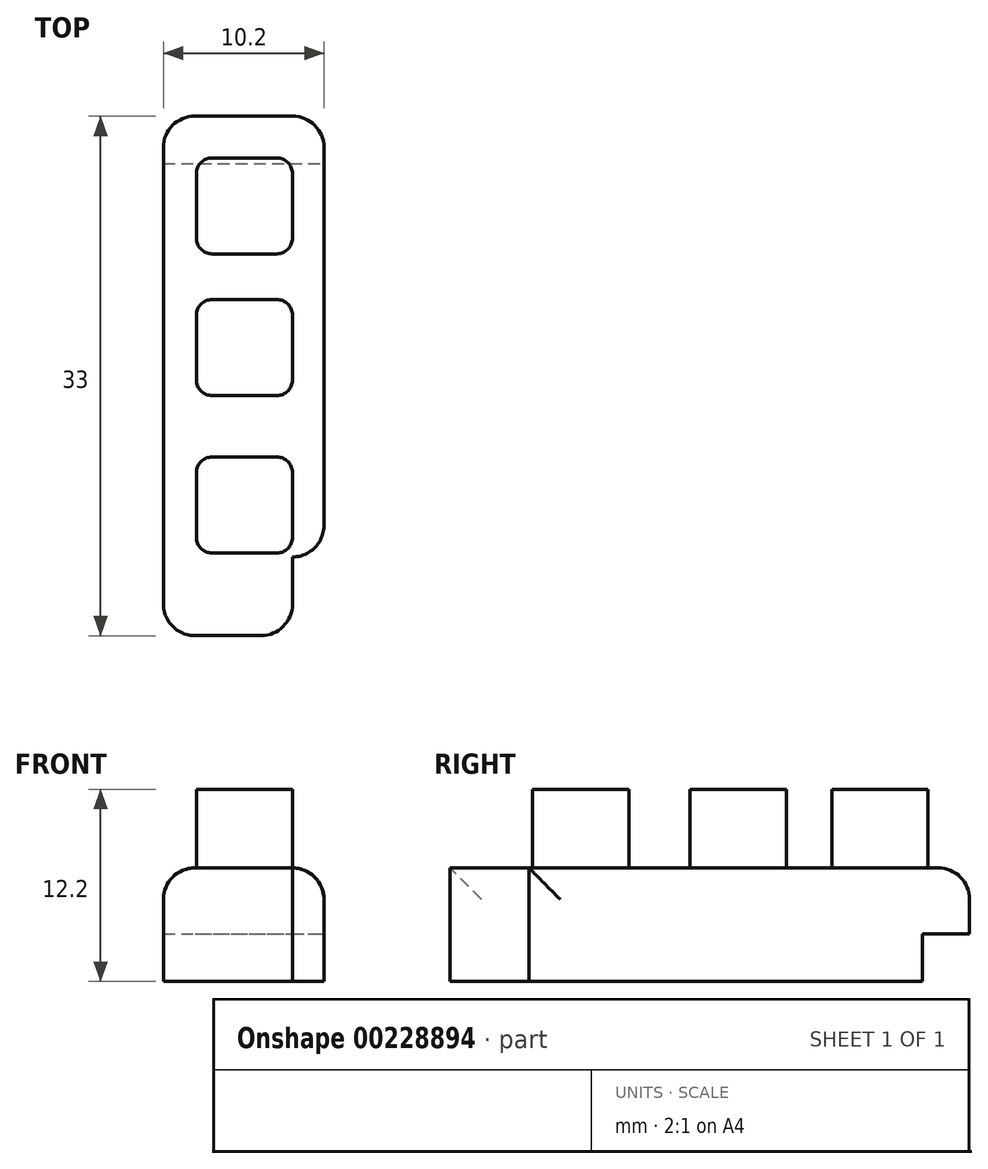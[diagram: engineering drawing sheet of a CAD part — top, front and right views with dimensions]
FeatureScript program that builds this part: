
annotation { "Feature Type Name" : "Feature", "Feature Type Description" : "" }
export const myFeature = defineFeature(function(context is Context, id is Id, definition is map)
    precondition{}
    {
        {
            var Q0;
            Q0=qCreatedBy(makeId("Top.planeOp"),FACE);
            var sketch = newSketch(context, id + "F0", { "sketchPlane" : qUnion([Q0])});
            skLineSegment(sketch, "E0.bottom", {"start": v(-1.8, 2.84) * mm, "end": v(4.4, 2.84) * mm});
            skLineSegment(sketch, "E0.left", {"start": v(-3.8, 0.84) * mm, "end": v(-3.8, -22.16) * mm});
            skLineSegment(sketch, "E0.right", {"start": v(6.4, 0.84) * mm, "end": v(6.4, -23.16) * mm});
            skPoint(sketch, "E1.visualSharp", {"position": v(-3.8, 2.84) * mm});
            skArc(sketch, "E1.filletArc", {"start": v(-1.8, 2.84) * mm, "mid": v(-3.22, 2.26) * mm, "end": v(-3.8, 0.84) * mm});
            skPoint(sketch, "E2.visualSharp", {"position": v(6.4, 2.84) * mm});
            skArc(sketch, "E2.filletArc", {"start": v(6.4, 0.84) * mm, "mid": v(5.8, 2.26) * mm, "end": v(4.4, 2.84) * mm});
            skPoint(sketch, "E3.visualSharp", {"position": v(6.4, -29.16) * mm});
            skLineSegment(sketch, "E4.top", {"start": v(-1.8, -30.16) * mm, "end": v(2.4, -30.16) * mm});
            skLineSegment(sketch, "E4.left", {"start": v(-3.8, -22.16) * mm, "end": v(-3.8, -28.16) * mm});
            skPoint(sketch, "E5.visualSharp", {"position": v(-3.8, -30.16) * mm});
            skArc(sketch, "E5.filletArc", {"start": v(-3.8, -28.16) * mm, "mid": v(-3.22, -29.57) * mm, "end": v(-1.8, -30.16) * mm});
            skLineSegment(sketch, "E6.bottom", {"start": v(4.4, -25.16) * mm, "end": v(4.4, -25.16) * mm});
            skLineSegment(sketch, "E6.right", {"start": v(4.4, -25.16) * mm, "end": v(4.4, -28.16) * mm});
            skPoint(sketch, "E7.visualSharp", {"position": v(6.4, -25.16) * mm});
            skArc(sketch, "E7.filletArc", {"start": v(4.4, -25.16) * mm, "mid": v(5.8, -24.57) * mm, "end": v(6.4, -23.16) * mm});
            skPoint(sketch, "E8.visualSharp", {"position": v(4.4, -30.16) * mm});
            skArc(sketch, "E8.filletArc", {"start": v(2.4, -30.16) * mm, "mid": v(3.8, -29.57) * mm, "end": v(4.4, -28.16) * mm});
            skSolve(sketch);
        }
        {
            var Q0;
            Q0 = qSketchRegion(id + "F0", true);
            extrude(context, id + "F1", {"entities" : qUnion([Q0]), "depth" : 7.2 * mm, "offsetDistance" : 25 * mm});
        }
        {
            var Q0;
            Q0=makeQuery(id+"F1.opExtrude","CAP_EDGE",EDGE,{"disambiguationData":[OSD([sQuery(id+"F0.wireOp",EDGE,"E0.left")])],"isStart":false});
            var Q1;
            Q1=makeQuery(id+"F1.opExtrude","CAP_EDGE",EDGE,{"disambiguationData":[OSD([sQuery(id+"F0.wireOp",EDGE,"E1.filletArc")])],"isStart":false});
            var Q2;
            Q2=makeQuery(id+"F1.opExtrude","CAP_EDGE",EDGE,{"disambiguationData":[OSD([sQuery(id+"F0.wireOp",EDGE,"E0.bottom")])],"isStart":false});
            var Q3;
            Q3=makeQuery(id+"F1.opExtrude","CAP_EDGE",EDGE,{"disambiguationData":[OSD([sQuery(id+"F0.wireOp",EDGE,"E0.right")])],"isStart":false});
            var Q4;
            Q4=makeQuery(id+"F1.opExtrude","CAP_EDGE",EDGE,{"disambiguationData":[OSD([sQuery(id+"F0.wireOp",EDGE,"E0.top")])],"isStart":false});
            var Q5;
            Q5=makeQuery(id+"F1.opExtrude","CAP_EDGE",EDGE,{"disambiguationData":[OSD([sQuery(id+"F0.wireOp",EDGE,"yFoGW2SI-jLqb-oOE9-2AmF-UsZTGsxdIEaI.right")])],"isStart":false});
            fillet(context, id + "F2", {"entities" : qUnion([Q0, Q1, Q2, Q3, Q4, Q5]), "radius" : 2 * mm, "defaultsChanged" : false, "vertexSettings" : [], "allowEdgeOverflow" : false});
        }
        {
            var Q0;
            Q0=makeQuery(id+"F1.opExtrude","CAP_FACE",FACE,{"disambiguationData":[OSD([sQuery(id+"F0.wireOp",EDGE,"E0.bottom"),sQuery(id+"F0.wireOp",EDGE,"E0.top"),sQuery(id+"F0.wireOp",EDGE,"E0.left"),sQuery(id+"F0.wireOp",EDGE,"E0.right"),sQuery(id+"F0.wireOp",EDGE,"yFoGW2SI-jLqb-oOE9-2AmF-UsZTGsxdIEaI.right"),sQuery(id+"F0.wireOp",EDGE,"E1.filletArc"),sQuery(id+"F0.wireOp",EDGE,"E2.filletArc"),sQuery(id+"F0.wireOp",EDGE,"E3.filletArc"),sQuery(id+"F0.wireOp",EDGE,"56ebe38a-3feb-4b89-9773-a585b812c94d.filletArc"),sQuery(id+"F0.wireOp",EDGE,"123d125b-be54-48a5-baf1-07878bb31a06.filletArc")])],"isStart":false});
            var sketch = newSketch(context, id + "F3", { "sketchPlane" : qUnion([Q0])});
            skLineSegment(sketch, "E9.bottom", {"start": v(-0.7, 0.2) * mm, "end": v(3.4, 0.2) * mm});
            skLineSegment(sketch, "E9.top", {"start": v(-0.7, -5.9) * mm, "end": v(3.4, -5.9) * mm});
            skLineSegment(sketch, "E9.left", {"start": v(-1.7, -0.8) * mm, "end": v(-1.7, -4.9) * mm});
            skLineSegment(sketch, "E9.right", {"start": v(4.4, -0.8) * mm, "end": v(4.4, -4.9) * mm});
            skLineSegment(sketch, "E10.bottom", {"start": v(-0.7, -8.8) * mm, "end": v(3.4, -8.8) * mm});
            skLineSegment(sketch, "E10.top", {"start": v(-0.7, -14.9) * mm, "end": v(3.4, -14.9) * mm});
            skLineSegment(sketch, "E10.left", {"start": v(-1.7, -9.8) * mm, "end": v(-1.7, -13.9) * mm});
            skLineSegment(sketch, "E10.right", {"start": v(4.4, -9.8) * mm, "end": v(4.4, -13.9) * mm});
            skLineSegment(sketch, "E11.bottom", {"start": v(-0.7, -18.8) * mm, "end": v(3.4, -18.8) * mm});
            skLineSegment(sketch, "E11.top", {"start": v(-0.7, -24.9) * mm, "end": v(3.4, -24.9) * mm});
            skLineSegment(sketch, "E11.left", {"start": v(-1.7, -19.8) * mm, "end": v(-1.7, -23.9) * mm});
            skLineSegment(sketch, "E11.right", {"start": v(4.4, -19.8) * mm, "end": v(4.4, -23.9) * mm});
            skPoint(sketch, "E12.visualSharp", {"position": v(-1.7, 0.2) * mm});
            skArc(sketch, "E12.filletArc", {"start": v(-0.7, 0.2) * mm, "mid": v(-1.41, -0.1) * mm, "end": v(-1.7, -0.8) * mm});
            skPoint(sketch, "E13.visualSharp", {"position": v(4.4, 0.2) * mm});
            skArc(sketch, "E13.filletArc", {"start": v(4.4, -0.8) * mm, "mid": v(4.1, -0.1) * mm, "end": v(3.4, 0.2) * mm});
            skPoint(sketch, "E14.visualSharp", {"position": v(4.4, -5.9) * mm});
            skArc(sketch, "E14.filletArc", {"start": v(3.4, -5.9) * mm, "mid": v(4.1, -5.61) * mm, "end": v(4.4, -4.9) * mm});
            skPoint(sketch, "E15.visualSharp", {"position": v(-1.7, -5.9) * mm});
            skArc(sketch, "E15.filletArc", {"start": v(-1.7, -4.9) * mm, "mid": v(-1.41, -5.61) * mm, "end": v(-0.7, -5.9) * mm});
            skPoint(sketch, "E16.visualSharp", {"position": v(4.4, -8.8) * mm});
            skArc(sketch, "E16.filletArc", {"start": v(4.4, -9.8) * mm, "mid": v(4.1, -9.1) * mm, "end": v(3.4, -8.8) * mm});
            skPoint(sketch, "E17.visualSharp", {"position": v(4.4, -14.9) * mm});
            skArc(sketch, "E17.filletArc", {"start": v(3.4, -14.9) * mm, "mid": v(4.1, -14.61) * mm, "end": v(4.4, -13.9) * mm});
            skPoint(sketch, "E18.visualSharp", {"position": v(-1.7, -14.9) * mm});
            skArc(sketch, "E18.filletArc", {"start": v(-1.7, -13.9) * mm, "mid": v(-1.41, -14.61) * mm, "end": v(-0.7, -14.9) * mm});
            skPoint(sketch, "E19.visualSharp", {"position": v(-1.7, -8.8) * mm});
            skArc(sketch, "E19.filletArc", {"start": v(-0.7, -8.8) * mm, "mid": v(-1.41, -9.1) * mm, "end": v(-1.7, -9.8) * mm});
            skPoint(sketch, "E20.visualSharp", {"position": v(4.4, -18.8) * mm});
            skArc(sketch, "E20.filletArc", {"start": v(4.4, -19.8) * mm, "mid": v(4.1, -19.1) * mm, "end": v(3.4, -18.8) * mm});
            skPoint(sketch, "E21.visualSharp", {"position": v(4.4, -24.9) * mm});
            skArc(sketch, "E21.filletArc", {"start": v(3.4, -24.9) * mm, "mid": v(4.1, -24.61) * mm, "end": v(4.4, -23.9) * mm});
            skPoint(sketch, "E22.visualSharp", {"position": v(-1.7, -24.9) * mm});
            skArc(sketch, "E22.filletArc", {"start": v(-1.7, -23.9) * mm, "mid": v(-1.41, -24.61) * mm, "end": v(-0.7, -24.9) * mm});
            skPoint(sketch, "E23.visualSharp", {"position": v(-1.7, -18.8) * mm});
            skArc(sketch, "E23.filletArc", {"start": v(-0.7, -18.8) * mm, "mid": v(-1.41, -19.1) * mm, "end": v(-1.7, -19.8) * mm});
            skSolve(sketch);
        }
        {
            var Q0;
            Q0 = qSketchRegion(id + "F3", true);
            extrude(context, id + "F4", {"entities" : qUnion([Q0]), "operationType" : NewBodyOperationType.ADD, "depth" : 5 * mm, "offsetDistance" : 25 * mm});
        }
        {
            var Q0;
            Q0=makeQuery(id+"F1.opExtrude","CAP_FACE",FACE,{"disambiguationData":[OSD([sQuery(id+"F0.wireOp",EDGE,"E0.bottom"),sQuery(id+"F0.wireOp",EDGE,"E0.left"),sQuery(id+"F0.wireOp",EDGE,"E0.right"),sQuery(id+"F0.wireOp",EDGE,"E1.filletArc"),sQuery(id+"F0.wireOp",EDGE,"E2.filletArc"),sQuery(id+"F0.wireOp",EDGE,"E4.top"),sQuery(id+"F0.wireOp",EDGE,"E4.left"),sQuery(id+"F0.wireOp",EDGE,"E5.filletArc"),sQuery(id+"F0.wireOp",EDGE,"E6.right"),sQuery(id+"F0.wireOp",EDGE,"E7.filletArc"),sQuery(id+"F0.wireOp",EDGE,"E8.filletArc")])],"isStart":true});
            var sketch = newSketch(context, id + "F5", { "sketchPlane" : qUnion([Q0])});
            skLineSegment(sketch, "E24.bottom", {"start": v(-3.8, 0.16) * mm, "end": v(6.4, 0.16) * mm});
            skLineSegment(sketch, "E24.top", {"start": v(-3.8, -2.84) * mm, "end": v(6.4, -2.84) * mm});
            skLineSegment(sketch, "E24.left", {"start": v(-3.8, 0.16) * mm, "end": v(-3.8, -2.84) * mm});
            skLineSegment(sketch, "E24.right", {"start": v(6.4, 0.16) * mm, "end": v(6.4, -2.84) * mm});
            skSolve(sketch);
        }
        {
            var Q0;
            Q0 = qSketchRegion(id + "F5", true);
            extrude(context, id + "F6", {"entities" : qUnion([Q0]), "operationType" : NewBodyOperationType.REMOVE, "oppositeDirection" : true, "depth" : 3 * mm, "offsetDistance" : 25 * mm});
        }
    });
